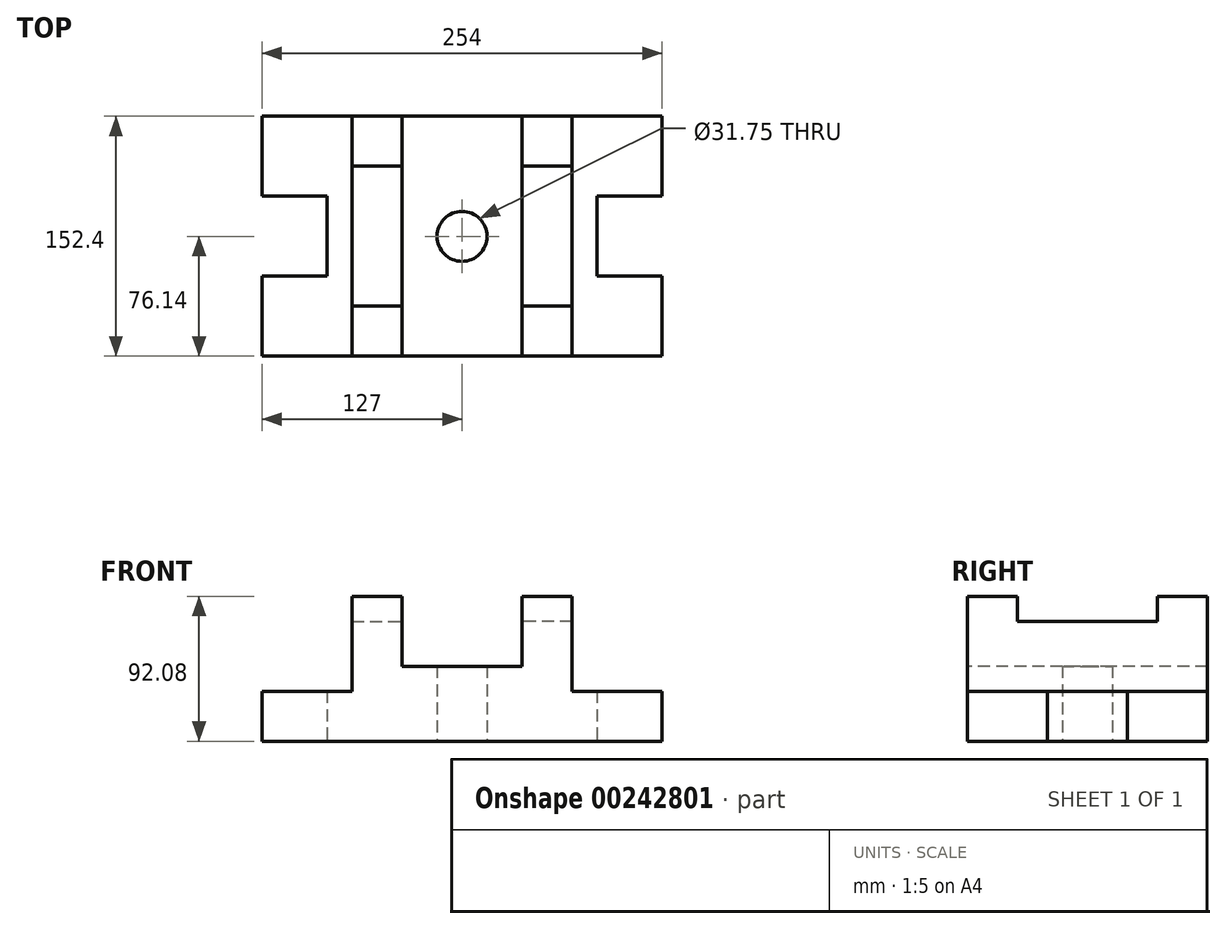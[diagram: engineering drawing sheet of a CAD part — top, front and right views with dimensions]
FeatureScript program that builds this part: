
annotation { "Feature Type Name" : "Feature", "Feature Type Description" : "" }
export const myFeature = defineFeature(function(context is Context, id is Id, definition is map)
    precondition{}
    {
        {
            var Q0;
            Q0=qCreatedBy(makeId("Top.planeOp"),FACE);
            var sketch = newSketch(context, id + "F0", { "sketchPlane" : qUnion([Q0])});
            skLineSegment(sketch, "E0", {"start": v(0, -76.14) * mm, "end": v(127, -76.14) * mm});
            skLineSegment(sketch, "E1", {"start": v(0, -76.14) * mm, "end": v(-127, -76.14) * mm});
            skLineSegment(sketch, "E2", {"start": v(-127, -76.14) * mm, "end": v(-127, -25.34) * mm});
            skLineSegment(sketch, "E3", {"start": v(-127, -25.34) * mm, "end": v(-85.72, -25.34) * mm});
            skLineSegment(sketch, "E4", {"start": v(-85.72, -25.34) * mm, "end": v(-85.72, 25.46) * mm});
            skLineSegment(sketch, "E5", {"start": v(-85.72, 25.46) * mm, "end": v(-127, 25.46) * mm});
            skLineSegment(sketch, "E6", {"start": v(-127, 25.46) * mm, "end": v(-127, 76.26) * mm});
            skLineSegment(sketch, "E7", {"start": v(-127, 76.26) * mm, "end": v(0, 76.26) * mm});
            skLineSegment(sketch, "E8", {"start": v(0, 76.26) * mm, "end": v(127, 76.26) * mm});
            skLineSegment(sketch, "E9", {"start": v(127, 76.26) * mm, "end": v(127, 25.46) * mm});
            skLineSegment(sketch, "E10", {"start": v(127, 25.46) * mm, "end": v(85.73, 25.46) * mm});
            skLineSegment(sketch, "E11", {"start": v(85.73, 25.46) * mm, "end": v(85.73, -25.34) * mm});
            skLineSegment(sketch, "E12", {"start": v(85.73, -25.34) * mm, "end": v(127, -25.34) * mm});
            skLineSegment(sketch, "E13", {"start": v(127, -25.34) * mm, "end": v(127, -76.14) * mm});
            skLineSegment(sketch, "E14", {"start": v(0, 76.26) * mm, "end": v(0, -76.14) * mm});
            skSolve(sketch);
        }
        {
            var Q0;
            Q0 = qSketchRegion(id + "F0", true);
            extrude(context, id + "F1", {"entities" : qUnion([Q0]), "depth" : 31.75 * mm});
        }
        {
            var Q0;
            Q0=makeQuery(id+"F1.opExtrude","CAP_FACE",FACE,{"disambiguationData":[OSD([sQuery(id+"F0.wireOp",EDGE,"E0"),sQuery(id+"F0.wireOp",EDGE,"E1"),sQuery(id+"F0.wireOp",EDGE,"E2"),sQuery(id+"F0.wireOp",EDGE,"E3"),sQuery(id+"F0.wireOp",EDGE,"E4"),sQuery(id+"F0.wireOp",EDGE,"E5"),sQuery(id+"F0.wireOp",EDGE,"E6"),sQuery(id+"F0.wireOp",EDGE,"E7"),sQuery(id+"F0.wireOp",EDGE,"E8"),sQuery(id+"F0.wireOp",EDGE,"E9"),sQuery(id+"F0.wireOp",EDGE,"E10"),sQuery(id+"F0.wireOp",EDGE,"E11"),sQuery(id+"F0.wireOp",EDGE,"E12"),sQuery(id+"F0.wireOp",EDGE,"E13")])],"isStart":false});
            var sketch = newSketch(context, id + "F2", { "sketchPlane" : qUnion([Q0])});
            skLineSegment(sketch, "E15", {"start": v(-127, 76.26) * mm, "end": v(-69.85, 76.26) * mm});
            skLineSegment(sketch, "E16", {"start": v(-127, -76.14) * mm, "end": v(-69.85, -76.14) * mm});
            skLineSegment(sketch, "E17", {"start": v(-69.85, -76.14) * mm, "end": v(-38.1, -76.14) * mm});
            skLineSegment(sketch, "E18", {"start": v(-69.85, 76.26) * mm, "end": v(-38.1, 76.26) * mm});
            skLineSegment(sketch, "E19", {"start": v(-69.85, 76.26) * mm, "end": v(-69.85, -76.14) * mm});
            skLineSegment(sketch, "E20", {"start": v(-38.1, 76.26) * mm, "end": v(-38.1, -76.14) * mm});
            skLineSegment(sketch, "E21", {"start": v(127, 76.26) * mm, "end": v(69.85, 76.26) * mm});
            skLineSegment(sketch, "E22", {"start": v(127, -76.14) * mm, "end": v(69.85, -76.14) * mm});
            skLineSegment(sketch, "E23", {"start": v(69.85, -76.14) * mm, "end": v(38.1, -76.14) * mm});
            skLineSegment(sketch, "E24", {"start": v(69.85, 76.26) * mm, "end": v(38.1, 76.26) * mm});
            skLineSegment(sketch, "E25", {"start": v(69.85, 76.26) * mm, "end": v(69.85, -76.14) * mm});
            skLineSegment(sketch, "E26", {"start": v(38.1, 76.26) * mm, "end": v(38.1, -76.14) * mm});
            skLineSegment(sketch, "E27", {"start": v(69.85, 76.26) * mm, "end": v(69.85, 44.51) * mm});
            skLineSegment(sketch, "E28", {"start": v(69.85, 44.51) * mm, "end": v(38.1, 44.51) * mm});
            skLineSegment(sketch, "E29", {"start": v(38.1, -76.14) * mm, "end": v(38.1, -44.39) * mm});
            skLineSegment(sketch, "E30", {"start": v(38.1, -44.39) * mm, "end": v(69.85, -44.39) * mm});
            skLineSegment(sketch, "E31", {"start": v(-69.85, 76.26) * mm, "end": v(-69.85, 44.51) * mm});
            skLineSegment(sketch, "E32", {"start": v(-69.85, 44.51) * mm, "end": v(-38.1, 44.51) * mm});
            skLineSegment(sketch, "E33", {"start": v(-69.85, -76.14) * mm, "end": v(-69.85, -44.39) * mm});
            skLineSegment(sketch, "E34", {"start": v(-69.85, -44.39) * mm, "end": v(-38.1, -44.39) * mm});
            skCircle(sketch, "E35", {"center": v(0, 0) * mm, "radius": 15.88 * mm});
            skSolve(sketch);
        }
        {
            var Q0;
            {var subQ0=sQuery(id+"F2.wireOp",EDGE,"E24");Q0=makeQuery(id+"F2.imprint","IMPRINT",FACE,{"disambiguationData":[TD([[makeQuery(id+"F2.imprint","IMPRINT",EDGE,{"derivedFrom":subQ0}),-1.0]])]});}
            extrude(context, id + "F3", {"entities" : qUnion([Q0]), "operationType" : NewBodyOperationType.ADD, "depth" : 60.32 * mm});
        }
        {
            var Q0;
            {var subQ0=sQuery(id+"F2.wireOp",EDGE,"E23");Q0=makeQuery(id+"F2.imprint","IMPRINT",FACE,{"disambiguationData":[TD([[makeQuery(id+"F2.imprint","IMPRINT",EDGE,{"derivedFrom":subQ0}),1.0]])]});}
            extrude(context, id + "F4", {"entities" : qUnion([Q0]), "operationType" : NewBodyOperationType.ADD, "depth" : 60.32 * mm});
        }
        {
            var Q0;
            {var subQ0=sQuery(id+"F2.wireOp",EDGE,"E17");Q0=makeQuery(id+"F2.imprint","IMPRINT",FACE,{"disambiguationData":[TD([[makeQuery(id+"F2.imprint","IMPRINT",EDGE,{"derivedFrom":subQ0}),1.0]])]});}
            extrude(context, id + "F5", {"entities" : qUnion([Q0]), "operationType" : NewBodyOperationType.ADD, "depth" : 60.32 * mm});
        }
        {
            var Q0;
            {var subQ0=sQuery(id+"F2.wireOp",EDGE,"E18");Q0=makeQuery(id+"F2.imprint","IMPRINT",FACE,{"disambiguationData":[TD([[makeQuery(id+"F2.imprint","IMPRINT",EDGE,{"derivedFrom":subQ0}),-1.0]])]});}
            extrude(context, id + "F6", {"entities" : qUnion([Q0]), "operationType" : NewBodyOperationType.ADD, "depth" : 60.32 * mm});
        }
        {
            var Q0;
            {var subQ0=sQuery(id+"F2.wireOp",EDGE,"E28");Q0=makeQuery(id+"F2.imprint","IMPRINT",FACE,{"disambiguationData":[TD([[makeQuery(id+"F2.imprint","IMPRINT",EDGE,{"derivedFrom":subQ0}),1.0]])]});}
            extrude(context, id + "F7", {"entities" : qUnion([Q0]), "operationType" : NewBodyOperationType.ADD, "depth" : 44.45 * mm});
        }
        {
            var Q0;
            Q0=makeQuery(id+"F2.imprint","IMPRINT",FACE,{"disambiguationData":[TD([[makeQuery(id+"F2.imprint","IMPRINT",EDGE,{"derivedFrom":sQuery(id+"F2.wireOp",EDGE,"E19")}),1.0]])]});
            extrude(context, id + "F8", {"entities" : qUnion([Q0]), "operationType" : NewBodyOperationType.ADD, "depth" : 44.45 * mm});
        }
        {
            var Q0;
            {var subQ6=sQuery(id+"F2.wireOp",EDGE,"E26");var subQ9=sQuery(id+"F0.wireOp",EDGE,"E1");var subQ10=sQuery(id+"F0.wireOp",EDGE,"E0");var subQ13=makeQuery(id+"F3.opExtrude","SWEPT_FACE",FACE,{"disambiguationData":[OSD([subQ6])]});var subQ14=sQuery(id+"F0.wireOp",EDGE,"E8");var subQ15=sQuery(id+"F0.wireOp",EDGE,"E7");var subQ17=sQuery(id+"F0.wireOp",EDGE,"E6");var subQ18=sQuery(id+"F0.wireOp",EDGE,"E5");var subQ19=sQuery(id+"F0.wireOp",EDGE,"E2");var subQ20=sQuery(id+"F0.wireOp",EDGE,"E3");var subQ21=sQuery(id+"F0.wireOp",EDGE,"E4");Q0=makeQuery(id+"F8.boolean.opBoolean","SPLIT",FACE,{"disambiguationData":[TD([subQ13])],"derivedFrom":makeQuery(id+"F7.boolean.opBoolean","SPLIT",FACE,{"disambiguationData":[TD([makeQuery(id+"F1.opExtrude","SWEPT_FACE",FACE,{"disambiguationData":[OSD([subQ19])]})])],"derivedFrom":makeQuery(id+"F1.opExtrude","CAP_FACE",FACE,{"disambiguationData":[OSD([subQ10,subQ9,subQ19,subQ20,subQ21,subQ18,subQ17,subQ15,subQ14,sQuery(id+"F0.wireOp",EDGE,"E9"),sQuery(id+"F0.wireOp",EDGE,"E10"),sQuery(id+"F0.wireOp",EDGE,"E11"),sQuery(id+"F0.wireOp",EDGE,"E12"),sQuery(id+"F0.wireOp",EDGE,"E13")])],"isStart":false})})});}
            extrude(context, id + "F9", {"entities" : qUnion([Q0]), "operationType" : NewBodyOperationType.ADD, "depth" : 15.88 * mm});
        }
        {
            var Q0;
            Q0=qCreatedBy(makeId("Top.planeOp"),FACE);
            var sketch = newSketch(context, id + "F10", { "sketchPlane" : qUnion([Q0])});
            skCircle(sketch, "E36", {"center": v(0, 0) * mm, "radius": 15.88 * mm});
            skSolve(sketch);
        }
        {
            var Q0;
            Q0=makeQuery(id+"F10.imprint","IMPRINT",FACE,{"disambiguationData":[TD([[makeQuery(id+"F10.imprint","IMPRINT",EDGE,{"derivedFrom":sQuery(id+"F10.wireOp",EDGE,"E36")}),1.0]])]});
            var Q1;
            Q1=sQuery(id+"F10.wireOp",EDGE,"E36");
            var Q2;
            Q2=sQuery(id+"F2.wireOp",EDGE,"E35");
            extrude(context, id + "F11", {"entities" : qUnion([Q0]), "operationType" : NewBodyOperationType.REMOVE, "surfaceEntities" : qUnion([Q1, Q2]), "depth" : 48.26 * mm});
        }
    });
